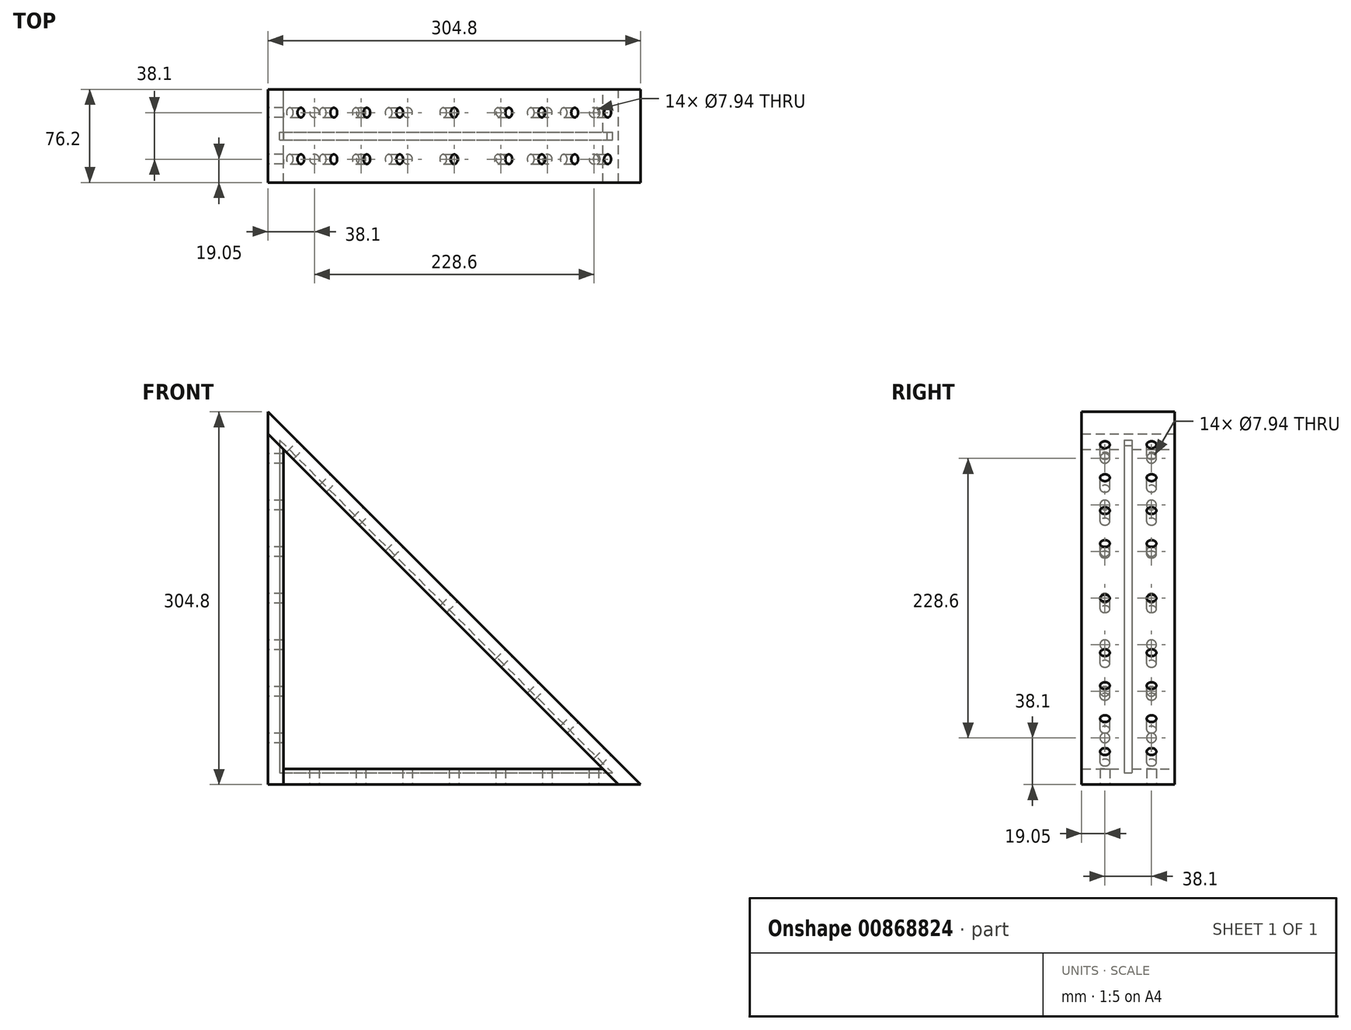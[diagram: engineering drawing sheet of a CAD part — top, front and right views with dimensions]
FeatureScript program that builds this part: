
annotation { "Feature Type Name" : "Feature", "Feature Type Description" : "" }
export const myFeature = defineFeature(function(context is Context, id is Id, definition is map)
    precondition{}
    {
        {
            var Q0;
            Q0=qCreatedBy(makeId("Front.planeOp"),FACE);
            var sketch = newSketch(context, id + "F0", { "sketchPlane" : qUnion([Q0])});
            skLineSegment(sketch, "E0.top", {"start": v(-152.4, -152.4) * mm, "end": v(152.4, -152.4) * mm});
            skLineSegment(sketch, "E0.left", {"start": v(-152.4, 152.4) * mm, "end": v(-152.4, -152.4) * mm});
            skPoint(sketch, "E0.middle", {"position": v(0, 0) * mm});
            skLineSegment(sketch, "E1", {"start": v(-152.4, 152.4) * mm, "end": v(152.4, -152.4) * mm});
            skPoint(sketch, "E0.right.start.orphan", {"position": v(152.4, 152.4) * mm});
            skLineSegment(sketch, "E2.0", {"start": v(-152.4, 134.44) * mm, "end": v(134.44, -152.4) * mm});
            skLineSegment(sketch, "E2.2", {"start": v(-139.7, -139.7) * mm, "end": v(121.74, -139.7) * mm});
            skLineSegment(sketch, "E3.0", {"start": v(-146.05, 137.07) * mm, "end": v(-146.05, -146.05) * mm});
            skLineSegment(sketch, "E3.1", {"start": v(-146.05, 137.07) * mm, "end": v(137.07, -146.05) * mm});
            skLineSegment(sketch, "E3.2", {"start": v(-146.05, -146.05) * mm, "end": v(137.07, -146.05) * mm});
            skPoint(sketch, "E4", {"position": v(-146.05, 101.6) * mm});
            skPoint(sketch, "E5", {"position": v(-146.05, 50.8) * mm});
            skPoint(sketch, "E6", {"position": v(-146.05, 0) * mm});
            skPoint(sketch, "E7", {"position": v(-146.05, -50.8) * mm});
            skPoint(sketch, "E8", {"position": v(-146.05, -101.6) * mm});
            skPoint(sketch, "E9", {"position": v(-101.6, -146.05) * mm});
            skPoint(sketch, "E10", {"position": v(-50.8, -146.05) * mm});
            skPoint(sketch, "E11", {"position": v(50.8, -146.05) * mm});
            skPoint(sketch, "E12", {"position": v(101.6, -146.05) * mm});
            skPoint(sketch, "E13", {"position": v(117.89, -126.87) * mm});
            skPoint(sketch, "E14", {"position": v(99.05, -108.03) * mm});
            skPoint(sketch, "E15", {"position": v(63.13, -72.1) * mm});
            skPoint(sketch, "E16", {"position": v(27.2, -36.19) * mm});
            skPoint(sketch, "E17", {"position": v(-8.72, -0.26) * mm});
            skPoint(sketch, "E18", {"position": v(-116.48, 107.5) * mm});
            skPoint(sketch, "E19", {"position": v(0, -146.05) * mm});
            skPoint(sketch, "E20", {"position": v(-80.56, 71.58) * mm});
            skPoint(sketch, "E21", {"position": v(-44.64, 35.66) * mm});
            skLineSegment(sketch, "E22.0", {"start": v(-142.88, 129.4) * mm, "end": v(-142.87, -142.87) * mm});
            skLineSegment(sketch, "E23.0", {"start": v(-142.87, 129.4) * mm, "end": v(129.4, -142.87) * mm});
            skLineSegment(sketch, "E24.0", {"start": v(-142.87, -142.87) * mm, "end": v(129.4, -142.87) * mm});
            skLineSegment(sketch, "E25.trimOffspring", {"start": v(-139.7, 121.74) * mm, "end": v(-139.7, -152.4) * mm});
            skPoint(sketch, "E26.orphan", {"position": v(-152.4, 143.42) * mm});
            skPoint(sketch, "E27.orphan", {"position": v(143.42, -152.4) * mm});
            skSolve(sketch);
        }
        {
            var Q0;
            {var subQ1=sQuery(id+"F0.wireOp",EDGE,"E1");var subQ5=sQuery(id+"F0.wireOp",EDGE,"E0.left");var subQ6=makeQuery(id+"F0.imprint","INTERSECT",VERTEX,{"derivedFrom":[subQ5,subQ1]});Q0=makeQuery(id+"F0.imprint","IMPRINT",FACE,{"disambiguationData":[TD([[makeQuery(id+"F0.imprint","IMPRINT",EDGE,{"disambiguationData":[TD([[subQ6,-1.0]])],"derivedFrom":subQ5}),1.0]])]});}
            var Q1;
            {var subQ0=sQuery(id+"F0.wireOp",EDGE,"E3.1");Q1=makeQuery(id+"F0.imprint","IMPRINT",FACE,{"disambiguationData":[TD([[makeQuery(id+"F0.imprint","IMPRINT",EDGE,{"derivedFrom":subQ0}),-1.0]])]});}
            var Q2;
            {var subQ0=sQuery(id+"F0.wireOp",EDGE,"E23.0");Q2=makeQuery(id+"F0.imprint","IMPRINT",FACE,{"disambiguationData":[TD([[makeQuery(id+"F0.imprint","IMPRINT",EDGE,{"derivedFrom":subQ0}),-1.0]])]});}
            extrude(context, id + "F1", {"entities" : qUnion([Q0, Q1, Q2]), "endBound" : BoundingType.SYMMETRIC, "depth" : 76.2 * mm, "offsetDistance" : 25.4 * mm});
        }
        {
            var Q0;
            {var subQ1=sQuery(id+"F0.wireOp",EDGE,"E0.left");var subQ9=sQuery(id+"F0.wireOp",EDGE,"E0.top");var subQ10=makeQuery(id+"F0.imprint","INTERSECT",VERTEX,{"derivedFrom":[subQ9,subQ1]});Q0=makeQuery(id+"F0.imprint","IMPRINT",FACE,{"disambiguationData":[TD([[makeQuery(id+"F0.imprint","IMPRINT",EDGE,{"disambiguationData":[TD([[subQ10,-1.0]])],"derivedFrom":subQ9}),1.0]])]});}
            var Q1;
            {var subQ3=sQuery(id+"F0.wireOp",EDGE,"E2.0");var subQ6=sQuery(id+"F0.wireOp",EDGE,"E3.0");var subQ8=makeQuery(id+"F0.imprint","INTERSECT",VERTEX,{"derivedFrom":[subQ3,subQ6]});Q1=makeQuery(id+"F0.imprint","IMPRINT",FACE,{"disambiguationData":[TD([[makeQuery(id+"F0.imprint","IMPRINT",EDGE,{"disambiguationData":[TD([[subQ8,-1.0]])],"derivedFrom":subQ3}),-1.0]])]});}
            var Q2;
            {var subQ0=sQuery(id+"F0.wireOp",EDGE,"E25.trimOffspring");var subQ2=sQuery(id+"F0.wireOp",EDGE,"E2.0");var subQ3=makeQuery(id+"F0.imprint","INTERSECT",VERTEX,{"derivedFrom":[subQ2,subQ0]});Q2=makeQuery(id+"F0.imprint","IMPRINT",FACE,{"disambiguationData":[TD([[makeQuery(id+"F0.imprint","IMPRINT",EDGE,{"disambiguationData":[TD([[subQ3,1.0]])],"derivedFrom":subQ2}),-1.0]])]});}
            extrude(context, id + "F2", {"entities" : qUnion([Q0, Q1, Q2]), "endBound" : BoundingType.SYMMETRIC, "depth" : 76.2 * mm, "offsetDistance" : 25.4 * mm});
        }
        {
            var Q0;
            {var subQ0=sQuery(id+"F0.wireOp",EDGE,"E2.2");Q0=makeQuery(id+"F0.imprint","IMPRINT",FACE,{"disambiguationData":[TD([[makeQuery(id+"F0.imprint","IMPRINT",EDGE,{"derivedFrom":subQ0}),-1.0]])]});}
            var Q1;
            {var subQ0=sQuery(id+"F0.wireOp",EDGE,"E24.0");var subQ1=sQuery(id+"F0.wireOp",EDGE,"E2.0");var subQ2=makeQuery(id+"F0.imprint","INTERSECT",VERTEX,{"derivedFrom":[subQ1,subQ0]});Q1=makeQuery(id+"F0.imprint","IMPRINT",FACE,{"disambiguationData":[TD([[makeQuery(id+"F0.imprint","IMPRINT",EDGE,{"disambiguationData":[TD([[subQ2,-1.0]])],"derivedFrom":subQ1}),-1.0]])]});}
            var Q2;
            {var subQ0=sQuery(id+"F0.wireOp",EDGE,"E2.0");var subQ1=sQuery(id+"F0.wireOp",EDGE,"E0.top");var subQ2=makeQuery(id+"F0.imprint","INTERSECT",VERTEX,{"derivedFrom":[subQ1,subQ0]});Q2=makeQuery(id+"F0.imprint","IMPRINT",FACE,{"disambiguationData":[TD([[makeQuery(id+"F0.imprint","IMPRINT",EDGE,{"disambiguationData":[TD([[subQ2,1.0]])],"derivedFrom":subQ1}),1.0]])]});}
            extrude(context, id + "F3", {"entities" : qUnion([Q0, Q1, Q2]), "endBound" : BoundingType.SYMMETRIC, "depth" : 76.2 * mm, "offsetDistance" : 25.4 * mm});
        }
        {
            var Q0;
            {var subQ0=sQuery(id+"F0.wireOp",EDGE,"E2.0");Q0=makeQuery(id+"F0.imprint","IMPRINT",FACE,{"disambiguationData":[TD([[makeQuery(id+"F0.imprint","IMPRINT",EDGE,{"derivedFrom":subQ0}),-1.0]])]});}
            var Q1;
            {var subQ0=sQuery(id+"F0.wireOp",EDGE,"E25.trimOffspring");var subQ2=sQuery(id+"F0.wireOp",EDGE,"E2.0");var subQ3=makeQuery(id+"F0.imprint","INTERSECT",VERTEX,{"derivedFrom":[subQ2,subQ0]});Q1=makeQuery(id+"F0.imprint","IMPRINT",FACE,{"disambiguationData":[TD([[makeQuery(id+"F0.imprint","IMPRINT",EDGE,{"disambiguationData":[TD([[subQ3,1.0]])],"derivedFrom":subQ2}),-1.0]])]});}
            var Q2;
            {var subQ0=sQuery(id+"F0.wireOp",EDGE,"E23.0");Q2=makeQuery(id+"F0.imprint","IMPRINT",FACE,{"disambiguationData":[TD([[makeQuery(id+"F0.imprint","IMPRINT",EDGE,{"derivedFrom":subQ0}),-1.0]])]});}
            var Q3;
            {var subQ0=sQuery(id+"F0.wireOp",EDGE,"E2.2");Q3=makeQuery(id+"F0.imprint","IMPRINT",FACE,{"disambiguationData":[TD([[makeQuery(id+"F0.imprint","IMPRINT",EDGE,{"derivedFrom":subQ0}),-1.0]])]});}
            extrude(context, id + "F4", {"entities" : qUnion([Q0, Q1, Q2, Q3]), "endBound" : BoundingType.SYMMETRIC, "depth" : 6.35 * mm, "offsetDistance" : 25.4 * mm});
        }
        {
            var Q0;
            Q0=makeQuery(id+"F4.opExtrude","SWEPT_BODY",BODY,{"disambiguationData":[OSD([sQuery(id+"F0.wireOp",EDGE,"E22.0"),sQuery(id+"F0.wireOp",EDGE,"E23.0"),sQuery(id+"F0.wireOp",EDGE,"E24.0")])]});
            var Q1;
            Q1=makeQuery(id+"F1.opExtrude","SWEPT_BODY",BODY,{"disambiguationData":[OSD([sQuery(id+"F0.wireOp",EDGE,"E0.top"),sQuery(id+"F0.wireOp",EDGE,"E0.left"),sQuery(id+"F0.wireOp",EDGE,"E1"),sQuery(id+"F0.wireOp",EDGE,"E2.0")])]});
            var Q2;
            Q2=makeQuery(id+"F2.opExtrude","SWEPT_BODY",BODY,{"disambiguationData":[OSD([sQuery(id+"F0.wireOp",EDGE,"E0.top"),sQuery(id+"F0.wireOp",EDGE,"E0.left"),sQuery(id+"F0.wireOp",EDGE,"E2.0"),sQuery(id+"F0.wireOp",EDGE,"E25.trimOffspring")])]});
            var Q3;
            Q3=makeQuery(id+"F3.opExtrude","SWEPT_BODY",BODY,{"disambiguationData":[OSD([sQuery(id+"F0.wireOp",EDGE,"E0.top"),sQuery(id+"F0.wireOp",EDGE,"E2.0"),sQuery(id+"F0.wireOp",EDGE,"E2.2"),sQuery(id+"F0.wireOp",EDGE,"E25.trimOffspring")])]});
            booleanBodies(context, id + "F5", {"operationType" : BooleanOperationType.SUBTRACTION, "tools" : qUnion([Q0]), "targets" : qUnion([Q1, Q2, Q3]), "keepTools" : true});
        }
        {
            var Q0;
            Q0=makeQuery(id+"F2.opExtrude","SWEPT_FACE",FACE,{"disambiguationData":[OSD([sQuery(id+"F0.wireOp",EDGE,"E0.left")])]});
            var sketch = newSketch(context, id + "F6", { "sketchPlane" : qUnion([Q0])});
            skLineSegment(sketch, "E28.0", {"start": v(38.1, 152.4) * mm, "end": v(-38.1, 152.4) * mm});
            skLineSegment(sketch, "E28.1", {"start": v(-38.1, 152.4) * mm, "end": v(-38.1, -152.4) * mm});
            skLineSegment(sketch, "E28.2", {"start": v(38.1, 152.4) * mm, "end": v(38.1, -152.4) * mm});
            skLineSegment(sketch, "E28.3", {"start": v(38.1, -152.4) * mm, "end": v(-38.1, -152.4) * mm});
            skPoint(sketch, "E29.orphan", {"position": v(-38.1, 134.44) * mm});
            skPoint(sketch, "E30.orphan", {"position": v(38.1, 134.44) * mm});
            skLineSegment(sketch, "E31.0", {"start": v(38.1, 134.44) * mm, "end": v(-38.1, 134.44) * mm});
            skLineSegment(sketch, "E32", {"start": v(-38.1, -139.7) * mm, "end": v(38.1, -139.7) * mm});
            skPoint(sketch, "E33", {"position": v(0, 152.4) * mm});
            skPoint(sketch, "E34", {"position": v(0, -139.7) * mm});
            skLineSegment(sketch, "E35", {"start": v(0, 152.4) * mm, "end": v(0, -139.7) * mm});
            skLineSegment(sketch, "E36", {"start": v(-19.05, 152.4) * mm, "end": v(-19.05, -139.7) * mm});
            skLineSegment(sketch, "E37", {"start": v(19.05, -139.7) * mm, "end": v(19.05, 134.44) * mm});
            skPoint(sketch, "E38", {"position": v(-19.05, 134.44) * mm});
            skPoint(sketch, "E39", {"position": v(-19.05, -114.3) * mm});
            skPoint(sketch, "E40", {"position": v(-19.05, -76.2) * mm});
            skPoint(sketch, "E41", {"position": v(-19.05, -38.1) * mm});
            skPoint(sketch, "E42", {"position": v(-19.05, 0) * mm});
            skPoint(sketch, "E43", {"position": v(-19.05, 76.2) * mm});
            skPoint(sketch, "E44", {"position": v(-19.05, 38.1) * mm});
            skPoint(sketch, "E45.0.1.0", {"position": v(-19.05, 114.3) * mm});
            skPoint(sketch, "E45.1.0.0", {"position": v(19.05, 114.3) * mm});
            skPoint(sketch, "E45.1.0.1", {"position": v(19.05, 76.2) * mm});
            skPoint(sketch, "E45.1.0.2", {"position": v(19.05, 38.1) * mm});
            skPoint(sketch, "E45.1.0.3", {"position": v(19.05, 0) * mm});
            skPoint(sketch, "E45.1.0.4", {"position": v(19.05, -38.1) * mm});
            skPoint(sketch, "E45.1.0.5", {"position": v(19.05, -76.2) * mm});
            skPoint(sketch, "E45.1.0.6", {"position": v(19.05, -114.3) * mm});
            skPoint(sketch, "E45.1.1.0", {"position": v(19.05, 114.3) * mm});
            skPoint(sketch, "E45.1.1.1", {"position": v(19.05, 76.2) * mm});
            skPoint(sketch, "E45.1.1.2", {"position": v(19.05, 38.1) * mm});
            skPoint(sketch, "E45.1.1.3", {"position": v(19.05, 0) * mm});
            skPoint(sketch, "E45.1.1.4", {"position": v(19.05, -38.1) * mm});
            skPoint(sketch, "E45.1.1.5", {"position": v(19.05, -76.2) * mm});
            skPoint(sketch, "E45.1.1.6", {"position": v(19.05, -114.3) * mm});
            skSolve(sketch);
        }
        {
            var Q0;
            Q0=makeQuery(id+"F3.opExtrude","SWEPT_FACE",FACE,{"disambiguationData":[OSD([sQuery(id+"F0.wireOp",EDGE,"E0.top")])]});
            var sketch = newSketch(context, id + "F7", { "sketchPlane" : qUnion([Q0])});
            skLineSegment(sketch, "E46.0", {"start": v(-152.4, 38.1) * mm, "end": v(-152.4, -38.1) * mm});
            skLineSegment(sketch, "E46.1", {"start": v(152.4, 38.1) * mm, "end": v(152.4, -38.1) * mm});
            skLineSegment(sketch, "E46.2", {"start": v(-152.4, 38.1) * mm, "end": v(134.44, 38.1) * mm});
            skLineSegment(sketch, "E46.3", {"start": v(-139.7, -38.1) * mm, "end": v(134.44, -38.1) * mm});
            skPoint(sketch, "E47.orphan", {"position": v(-139.7, 38.1) * mm});
            skLineSegment(sketch, "E48", {"start": v(-152.4, 19.05) * mm, "end": v(152.4, 19.05) * mm});
            skLineSegment(sketch, "E49", {"start": v(-152.4, -19.05) * mm, "end": v(152.4, -19.05) * mm});
            skPoint(sketch, "E50", {"position": v(-152.4, 19.05) * mm});
            skPoint(sketch, "E51", {"position": v(-152.4, -19.05) * mm});
            skPoint(sketch, "E52.1.0.0", {"position": v(-114.3, -19.05) * mm});
            skPoint(sketch, "E52.1.1.0", {"position": v(-114.3, 19.05) * mm});
            skPoint(sketch, "E52.2.0.0", {"position": v(-76.2, -19.05) * mm});
            skPoint(sketch, "E52.2.1.0", {"position": v(-76.2, 19.05) * mm});
            skPoint(sketch, "E52.3.0.0", {"position": v(-38.1, -19.05) * mm});
            skPoint(sketch, "E52.3.1.0", {"position": v(-38.1, 19.05) * mm});
            skPoint(sketch, "E52.4.0.0", {"position": v(0, -19.05) * mm});
            skPoint(sketch, "E52.4.1.0", {"position": v(0, 19.05) * mm});
            skPoint(sketch, "E52.5.0.0", {"position": v(38.1, -19.05) * mm});
            skPoint(sketch, "E52.5.1.0", {"position": v(38.1, 19.05) * mm});
            skPoint(sketch, "E52.6.0.0", {"position": v(76.2, -19.05) * mm});
            skPoint(sketch, "E52.6.1.0", {"position": v(76.2, 19.05) * mm});
            skPoint(sketch, "E52.7.0.0", {"position": v(114.3, -19.05) * mm});
            skPoint(sketch, "E52.7.1.0", {"position": v(114.3, 19.05) * mm});
            skLineSegment(sketch, "E52.direction1", {"start": v(-152.4, -19.05) * mm, "end": v(-114.3, -19.05) * mm, "construction": true});
            skLineSegment(sketch, "E52.direction2", {"start": v(-152.4, -19.05) * mm, "end": v(-152.4, 19.05) * mm, "construction": true});
            skSolve(sketch);
        }
        {
            var Q0;
            Q0=makeQuery(id+"F1.opExtrude","SWEPT_FACE",FACE,{"disambiguationData":[OSD([sQuery(id+"F0.wireOp",EDGE,"E1")])]});
            var sketch = newSketch(context, id + "F8", { "sketchPlane" : qUnion([Q0])});
            skPoint(sketch, "E53", {"position": v(19.05, 215.53) * mm});
            skPoint(sketch, "E54", {"position": v(19.05, -215.53) * mm});
            skPoint(sketch, "E55", {"position": v(19.05, 0) * mm});
            skPoint(sketch, "E55.positionSnap0", {"position": v(38.1, 0) * mm});
            skPoint(sketch, "E56.0.1.0", {"position": v(19.05, 177.43) * mm});
            skPoint(sketch, "E56.1.0.0", {"position": v(-19.05, 215.53) * mm});
            skPoint(sketch, "E56.1.1.0", {"position": v(-19.05, 177.43) * mm});
            skLineSegment(sketch, "E56.direction1", {"start": v(-19.05, 215.53) * mm, "end": v(19.05, 215.53) * mm, "construction": true});
            skLineSegment(sketch, "E56.direction2", {"start": v(19.05, 215.53) * mm, "end": v(19.05, 177.43) * mm, "construction": true});
            skPoint(sketch, "E57.0.0.2", {"position": v(19.05, 139.33) * mm});
            skPoint(sketch, "E57.0.0.3", {"position": v(19.05, 101.23) * mm});
            skPoint(sketch, "E57.0.1.2", {"position": v(-19.05, 139.33) * mm});
            skPoint(sketch, "E57.0.1.3", {"position": v(-19.05, 101.23) * mm});
            skPoint(sketch, "E58.0.0.4", {"position": v(19.05, 63.13) * mm});
            skPoint(sketch, "E58.0.1.4", {"position": v(-19.05, 63.13) * mm});
            skPoint(sketch, "E59.0.0.5", {"position": v(19.05, 25.03) * mm});
            skPoint(sketch, "E59.0.1.5", {"position": v(-19.05, 25.03) * mm});
            skLineSegment(sketch, "E60", {"start": v(0, 0) * mm, "end": v(165.44, 0) * mm});
            skPoint(sketch, "E61.MirrorP", {"position": v(19.05, -139.33) * mm});
            skPoint(sketch, "E62.MirrorP", {"position": v(-19.05, -177.43) * mm});
            skPoint(sketch, "E63.MirrorP", {"position": v(-19.05, -139.33) * mm});
            skPoint(sketch, "E64.MirrorP", {"position": v(-19.05, -101.23) * mm});
            skPoint(sketch, "E65.MirrorP", {"position": v(19.05, -101.23) * mm});
            skPoint(sketch, "E66.MirrorP", {"position": v(19.05, -63.13) * mm});
            skPoint(sketch, "E67.MirrorP", {"position": v(-19.05, -63.13) * mm});
            skPoint(sketch, "E68.MirrorP", {"position": v(19.05, -177.43) * mm});
            skPoint(sketch, "E69.MirrorP", {"position": v(19.05, -25.03) * mm});
            skPoint(sketch, "E70.MirrorP", {"position": v(-19.05, -25.03) * mm});
            skPoint(sketch, "E71", {"position": v(-19.05, 0) * mm});
            skPoint(sketch, "E72", {"position": v(0, 19.05) * mm});
            skPoint(sketch, "E73", {"position": v(0, -19.05) * mm});
            skSolve(sketch);
        }
        {
            var Q0;
            Q0=sQuery(id+"F6.wireOp",VERTEX,"E45.1.0.0");
            var Q1;
            Q1=sQuery(id+"F6.wireOp",VERTEX,"E45.1.0.1");
            var Q2;
            Q2=sQuery(id+"F6.wireOp",VERTEX,"E43");
            var Q3;
            Q3=sQuery(id+"F6.wireOp",VERTEX,"E44");
            var Q4;
            Q4=sQuery(id+"F6.wireOp",VERTEX,"E45.1.0.2");
            var Q5;
            Q5=sQuery(id+"F6.wireOp",VERTEX,"E45.1.0.3");
            var Q6;
            Q6=sQuery(id+"F6.wireOp",VERTEX,"E42");
            var Q7;
            Q7=sQuery(id+"F6.wireOp",VERTEX,"E41");
            var Q8;
            Q8=sQuery(id+"F6.wireOp",VERTEX,"E45.1.0.4");
            var Q9;
            Q9=sQuery(id+"F6.wireOp",VERTEX,"E45.1.0.5");
            var Q10;
            Q10=sQuery(id+"F6.wireOp",VERTEX,"E40");
            var Q11;
            Q11=sQuery(id+"F6.wireOp",VERTEX,"E39");
            var Q12;
            Q12=sQuery(id+"F6.wireOp",VERTEX,"E45.1.0.6");
            var Q13;
            Q13=sQuery(id+"F7.wireOp",VERTEX,"E52.1.1.0");
            var Q14;
            Q14=sQuery(id+"F7.wireOp",VERTEX,"E52.direction1.end");
            var Q15;
            Q15=sQuery(id+"F7.wireOp",VERTEX,"E52.2.0.0");
            var Q16;
            Q16=sQuery(id+"F7.wireOp",VERTEX,"E52.2.1.0");
            var Q17;
            Q17=sQuery(id+"F7.wireOp",VERTEX,"E52.3.1.0");
            var Q18;
            Q18=sQuery(id+"F7.wireOp",VERTEX,"E52.3.0.0");
            var Q19;
            Q19=sQuery(id+"F7.wireOp",VERTEX,"E52.4.1.0");
            var Q20;
            Q20=sQuery(id+"F7.wireOp",VERTEX,"E52.5.1.0");
            var Q21;
            Q21=sQuery(id+"F7.wireOp",VERTEX,"E52.6.1.0");
            var Q22;
            Q22=sQuery(id+"F7.wireOp",VERTEX,"E52.7.1.0");
            var Q23;
            Q23=sQuery(id+"F7.wireOp",VERTEX,"E52.7.0.0");
            var Q24;
            Q24=sQuery(id+"F7.wireOp",VERTEX,"E52.6.0.0");
            var Q25;
            Q25=sQuery(id+"F7.wireOp",VERTEX,"E52.5.0.0");
            var Q26;
            Q26=sQuery(id+"F7.wireOp",VERTEX,"E52.4.0.0");
            var Q27;
            Q27=sQuery(id+"F6.wireOp",VERTEX,"E45.0.1.0");
            var Q28;
            Q28=makeQuery(id+"F2.opExtrude","SWEPT_BODY",BODY,{"disambiguationData":[OSD([sQuery(id+"F0.wireOp",EDGE,"E0.top"),sQuery(id+"F0.wireOp",EDGE,"E0.left"),sQuery(id+"F0.wireOp",EDGE,"E2.0"),sQuery(id+"F0.wireOp",EDGE,"E25.trimOffspring")])]});
            var Q29;
            Q29=makeQuery(id+"F3.opExtrude","SWEPT_BODY",BODY,{"disambiguationData":[OSD([sQuery(id+"F0.wireOp",EDGE,"E0.top"),sQuery(id+"F0.wireOp",EDGE,"E2.0"),sQuery(id+"F0.wireOp",EDGE,"E2.2"),sQuery(id+"F0.wireOp",EDGE,"E25.trimOffspring")])]});
            hole(context, id + "F9", {"style" : HoleStyle.SIMPLE, "endStyle" : HoleEndStyle.THROUGH, "standardTappedOrClearance" : lookupTablePath({ "standard" : "ANSI", "engagement" : "75%", "pitch" : "16 tpi", "size" : "3/8", "type" : "Tapped" }), "standardBlindInLast" : lookupTablePath({ "standard" : "ANSI", "engagement" : "75%", "pitch" : "16 tpi", "size" : "3/8", "type" : "Tapped" }), "holeDiameter" : 7.94 * mm, "majorDiameter" : 9.52 * mm, "showTappedDepth" : true, "tappedDepth" : 12.7 * mm, "tapClearance" : 3, "startFromSketch" : true, "locations" : qUnion([Q0, Q1, Q2, Q3, Q4, Q5, Q6, Q7, Q8, Q9, Q10, Q11, Q12, Q13, Q14, Q15, Q16, Q17, Q18, Q19, Q20, Q21, Q22, Q23, Q24, Q25, Q26, Q27]), "scope" : qUnion([Q28, Q29])});
        }
        {
            var Q0;
            Q0=sQuery(id+"F8.wireOp",VERTEX,"E56.0.1.0");
            var Q1;
            Q1=sQuery(id+"F8.wireOp",VERTEX,"E56.1.1.0");
            var Q2;
            Q2=sQuery(id+"F8.wireOp",VERTEX,"E57.0.1.2");
            var Q3;
            Q3=sQuery(id+"F8.wireOp",VERTEX,"E57.0.0.2");
            var Q4;
            Q4=sQuery(id+"F8.wireOp",VERTEX,"E57.0.0.3");
            var Q5;
            Q5=sQuery(id+"F8.wireOp",VERTEX,"E57.0.1.3");
            var Q6;
            Q6=sQuery(id+"F8.wireOp",VERTEX,"E58.0.0.4");
            var Q7;
            Q7=sQuery(id+"F8.wireOp",VERTEX,"E58.0.1.4");
            var Q8;
            Q8=sQuery(id+"F8.wireOp",VERTEX,"E55");
            var Q9;
            Q9=sQuery(id+"F8.wireOp",VERTEX,"E67.MirrorP");
            var Q10;
            Q10=sQuery(id+"F8.wireOp",VERTEX,"E64.MirrorP");
            var Q11;
            Q11=sQuery(id+"F8.wireOp",VERTEX,"E63.MirrorP");
            var Q12;
            Q12=sQuery(id+"F8.wireOp",VERTEX,"E62.MirrorP");
            var Q13;
            Q13=sQuery(id+"F8.wireOp",VERTEX,"E68.MirrorP");
            var Q14;
            Q14=sQuery(id+"F8.wireOp",VERTEX,"E61.MirrorP");
            var Q15;
            Q15=sQuery(id+"F8.wireOp",VERTEX,"E65.MirrorP");
            var Q16;
            Q16=sQuery(id+"F8.wireOp",VERTEX,"E66.MirrorP");
            var Q17;
            Q17=sQuery(id+"F8.wireOp",VERTEX,"E71");
            var Q18;
            Q18=makeQuery(id+"F1.opExtrude","SWEPT_BODY",BODY,{"disambiguationData":[OSD([sQuery(id+"F0.wireOp",EDGE,"E0.top"),sQuery(id+"F0.wireOp",EDGE,"E0.left"),sQuery(id+"F0.wireOp",EDGE,"E1"),sQuery(id+"F0.wireOp",EDGE,"E2.0")])]});
            hole(context, id + "F10", {"style" : HoleStyle.SIMPLE, "endStyle" : HoleEndStyle.THROUGH, "standardTappedOrClearance" : lookupTablePath({ "standard" : "ANSI", "engagement" : "75%", "pitch" : "16 tpi", "size" : "3/8", "type" : "Tapped" }), "standardBlindInLast" : lookupTablePath({ "standard" : "ANSI", "engagement" : "75%", "pitch" : "16 tpi", "size" : "3/8", "type" : "Tapped" }), "holeDiameter" : 7.94 * mm, "majorDiameter" : 9.52 * mm, "showTappedDepth" : true, "tappedDepth" : 12.7 * mm, "tapClearance" : 3, "startFromSketch" : true, "locations" : qUnion([Q0, Q1, Q2, Q3, Q4, Q5, Q6, Q7, Q8, Q9, Q10, Q11, Q12, Q13, Q14, Q15, Q16, Q17]), "scope" : qUnion([Q18])});
        }
    });
